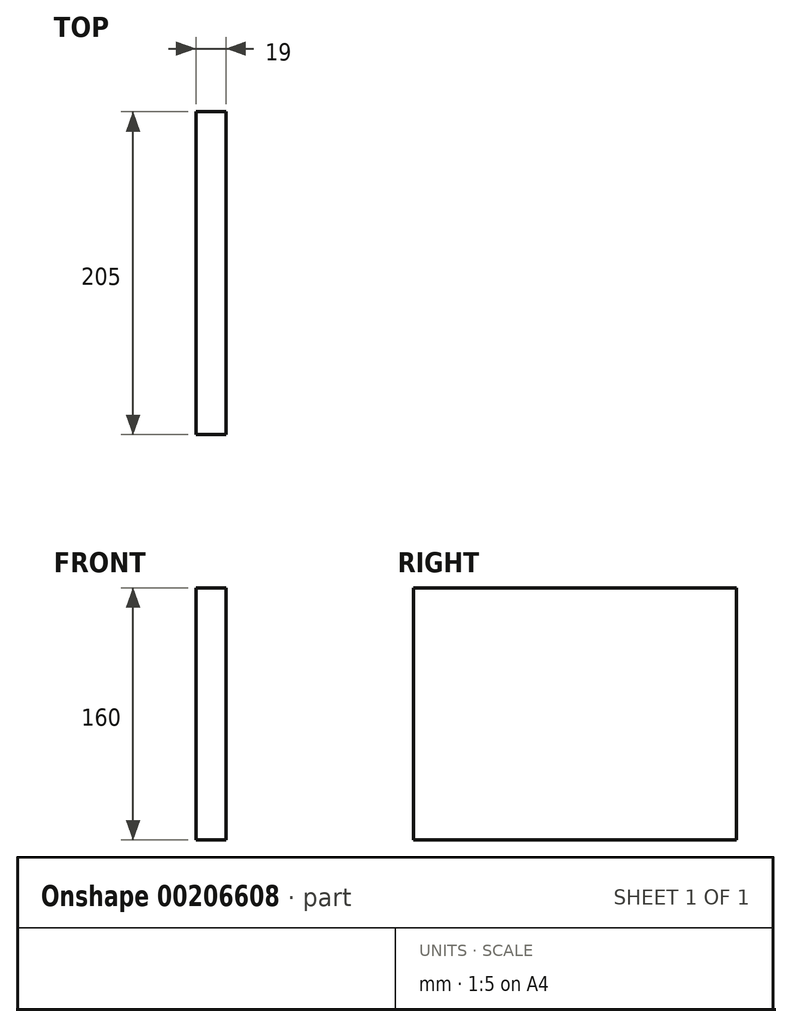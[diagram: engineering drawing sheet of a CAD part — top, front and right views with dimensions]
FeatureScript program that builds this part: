
annotation { "Feature Type Name" : "Feature", "Feature Type Description" : "" }
export const myFeature = defineFeature(function(context is Context, id is Id, definition is map)
    precondition{}
    {
        {
            var Q0;
            Q0=qCreatedBy(makeId("Front.planeOp"),FACE);
            var sketch = newSketch(context, id + "F0", { "sketchPlane" : qUnion([Q0])});
            skLineSegment(sketch, "E0.bottom", {"start": v(0, 0) * mm, "end": v(19, 0) * mm});
            skLineSegment(sketch, "E0.top", {"start": v(0, 160) * mm, "end": v(19, 160) * mm});
            skLineSegment(sketch, "E0.left", {"start": v(0, 0) * mm, "end": v(0, 160) * mm});
            skLineSegment(sketch, "E0.right", {"start": v(19, 0) * mm, "end": v(19, 160) * mm});
            skSolve(sketch);
        }
        {
            var Q0;
            Q0 = qSketchRegion(id + "F0", true);
            extrude(context, id + "F1", {"entities" : qUnion([Q0]), "depth" : 205 * mm});
        }
    });
